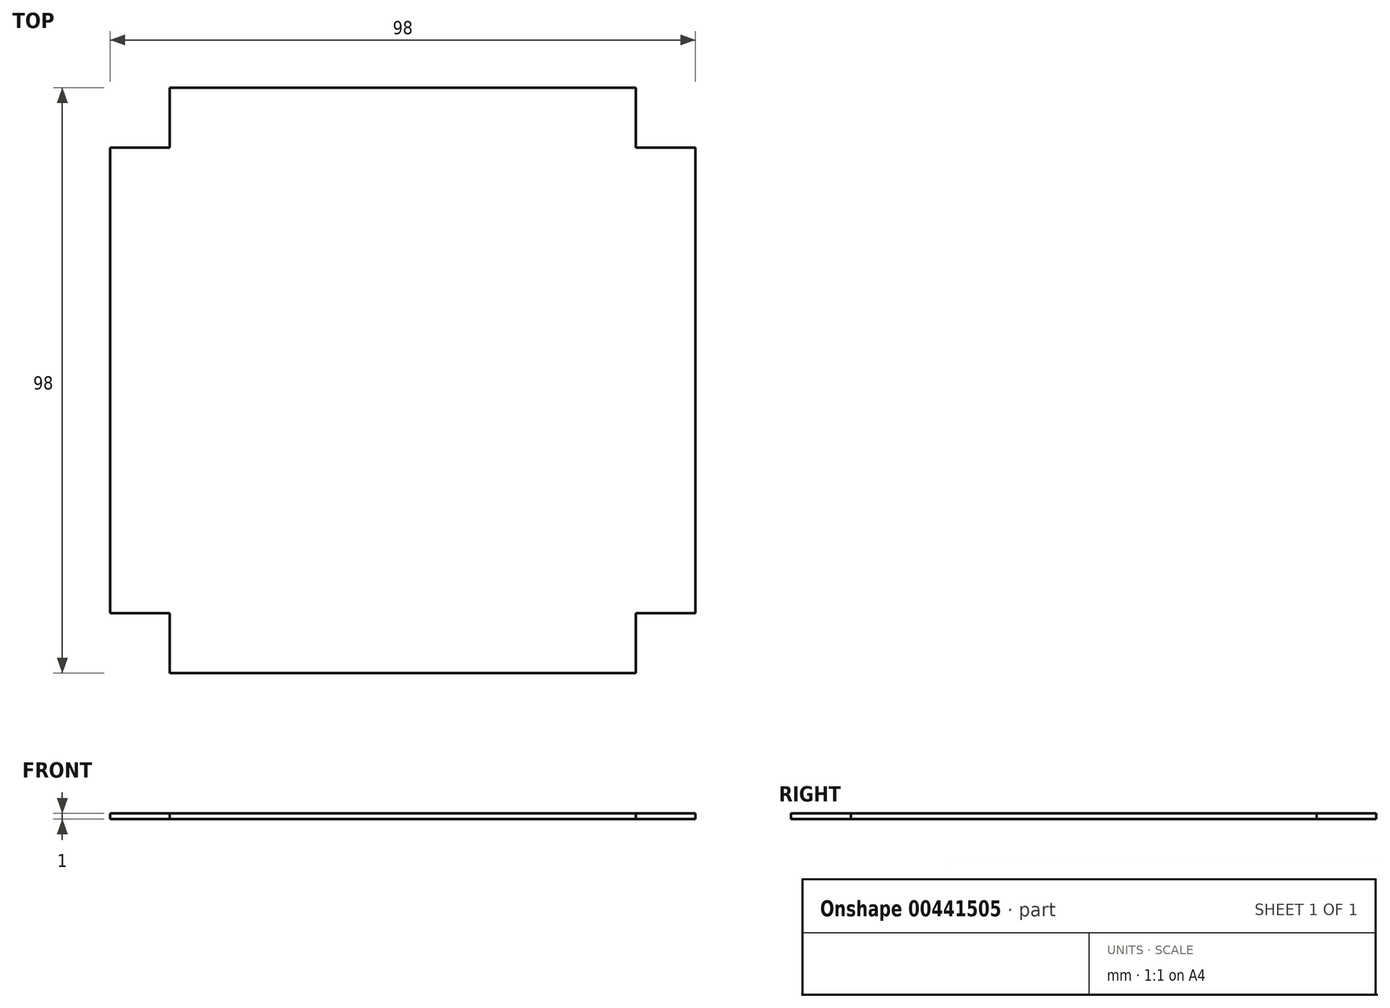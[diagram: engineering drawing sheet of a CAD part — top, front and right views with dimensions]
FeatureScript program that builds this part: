
annotation { "Feature Type Name" : "Feature", "Feature Type Description" : "" }
export const myFeature = defineFeature(function(context is Context, id is Id, definition is map)
    precondition{}
    {
        {
            var Q0;
            Q0=qCreatedBy(makeId("Top.planeOp"),FACE);
            var sketch = newSketch(context, id + "F0", { "sketchPlane" : qUnion([Q0])});
            skLineSegment(sketch, "E0.bottom", {"start": v(-39, 48) * mm, "end": v(39, 48) * mm});
            skLineSegment(sketch, "E0.top", {"start": v(-39, -50) * mm, "end": v(39, -50) * mm});
            skLineSegment(sketch, "E0.left", {"start": v(-49, 38) * mm, "end": v(-49, -40) * mm});
            skLineSegment(sketch, "E0.right", {"start": v(49, 38) * mm, "end": v(49, -40) * mm});
            skLineSegment(sketch, "E1", {"start": v(-49, 38) * mm, "end": v(-39, 38) * mm});
            skLineSegment(sketch, "E2", {"start": v(-39, 38) * mm, "end": v(-39, 48) * mm});
            skLineSegment(sketch, "E3.1.0", {"start": v(-39, -50) * mm, "end": v(-39, -40) * mm});
            skLineSegment(sketch, "E3.1.1", {"start": v(-39, -40) * mm, "end": v(-49, -40) * mm});
            skLineSegment(sketch, "E3.2.0", {"start": v(49, -40) * mm, "end": v(39, -40) * mm});
            skLineSegment(sketch, "E3.2.1", {"start": v(39, -40) * mm, "end": v(39, -50) * mm});
            skLineSegment(sketch, "E3.3.0", {"start": v(39, 48) * mm, "end": v(39, 38) * mm});
            skLineSegment(sketch, "E3.3.1", {"start": v(39, 38) * mm, "end": v(49, 38) * mm});
            skPoint(sketch, "E3.center", {"position": v(0, -1) * mm});
            skSolve(sketch);
        }
        {
            var Q0;
            Q0 = qSketchRegion(id + "F0", true);
            extrude(context, id + "F1", {"entities" : qUnion([Q0]), "depth" : 1 * mm});
        }
    });
